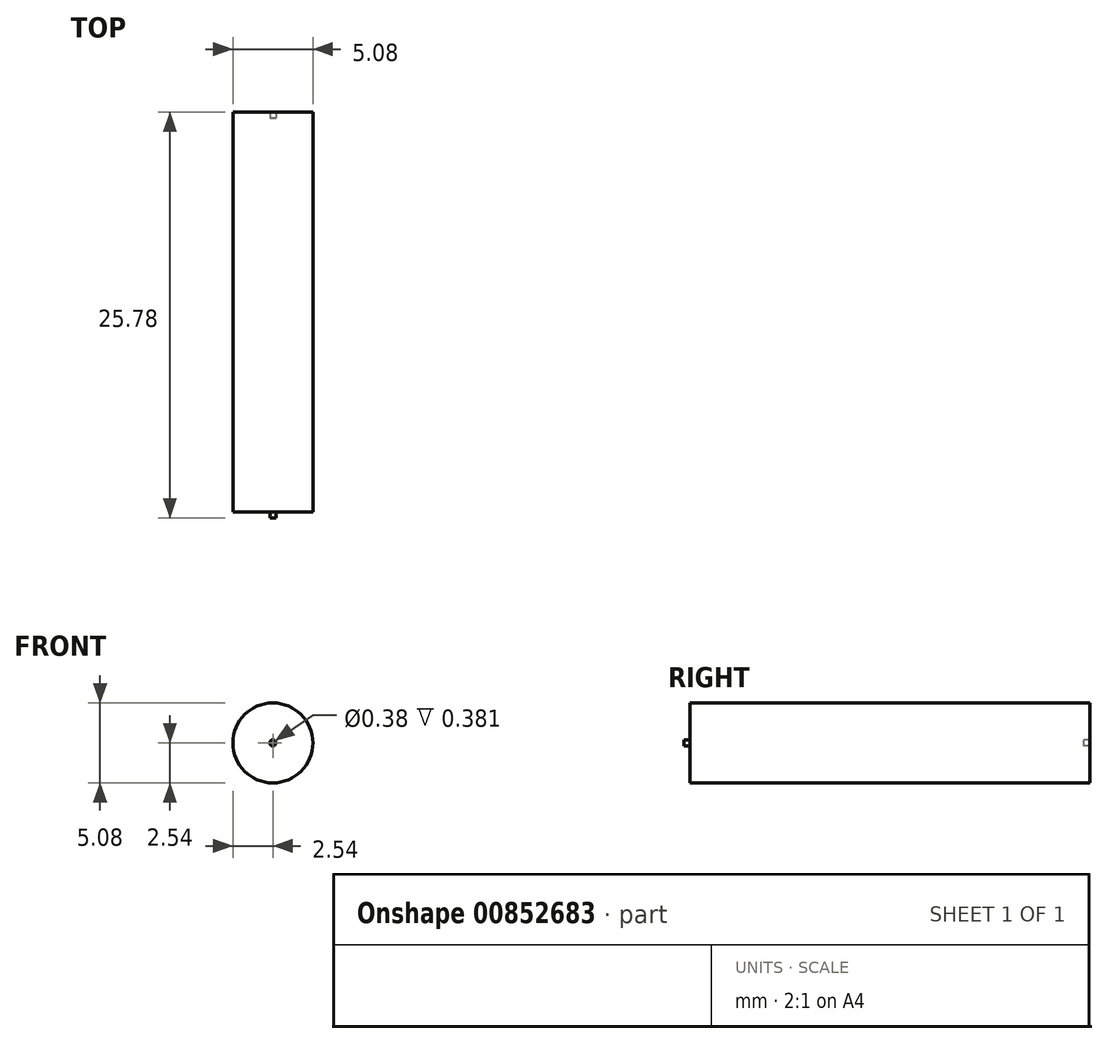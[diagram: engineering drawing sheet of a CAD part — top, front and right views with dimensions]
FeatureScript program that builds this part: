
annotation { "Feature Type Name" : "Feature", "Feature Type Description" : "" }
export const myFeature = defineFeature(function(context is Context, id is Id, definition is map)
    precondition{}
    {
        {
            var Q0;
            Q0=qCreatedBy(makeId("Front.planeOp"),FACE);
            var sketch = newSketch(context, id + "F0", { "sketchPlane" : qUnion([Q0])});
            skCircle(sketch, "E0", {"center": v(0, 0) * mm, "radius": 2.54 * mm});
            skCircle(sketch, "E1", {"center": v(0, 0) * mm, "radius": 0.2 * mm});
            skSolve(sketch);
        }
        {
            var Q0;
            Q0=makeQuery(id+"F0.imprint","IMPRINT",FACE,{"disambiguationData":[TD([[makeQuery(id+"F0.imprint","IMPRINT",EDGE,{"derivedFrom":sQuery(id+"F0.wireOp",EDGE,"E1")}),1.0]])]});
            extrude(context, id + "F1", {"entities" : qUnion([Q0]), "depth" : 0.38 * mm, "offsetDistance" : 25.4 * mm});
        }
        {
            var Q0;
            Q0=makeQuery(id+"F0.imprint","IMPRINT",FACE,{"disambiguationData":[TD([[makeQuery(id+"F0.imprint","IMPRINT",EDGE,{"derivedFrom":sQuery(id+"F0.wireOp",EDGE,"E0")}),1.0]])]});
            extrude(context, id + "F2", {"entities" : qUnion([Q0]), "operationType" : NewBodyOperationType.ADD, "oppositeDirection" : true, "depth" : 25.4 * mm, "offsetDistance" : 25.4 * mm});
        }
        {
            var Q0;
            Q0=makeQuery(id+"F1.opExtrude","CAP_FACE",FACE,{"disambiguationData":[OSD([sQuery(id+"F0.wireOp",EDGE,"E1")])],"isStart":false});
            extrude(context, id + "F3", {"entities" : qUnion([Q0]), "operationType" : NewBodyOperationType.ADD, "oppositeDirection" : true, "depth" : 25.4 * mm, "offsetDistance" : 25.4 * mm});
        }
    });
